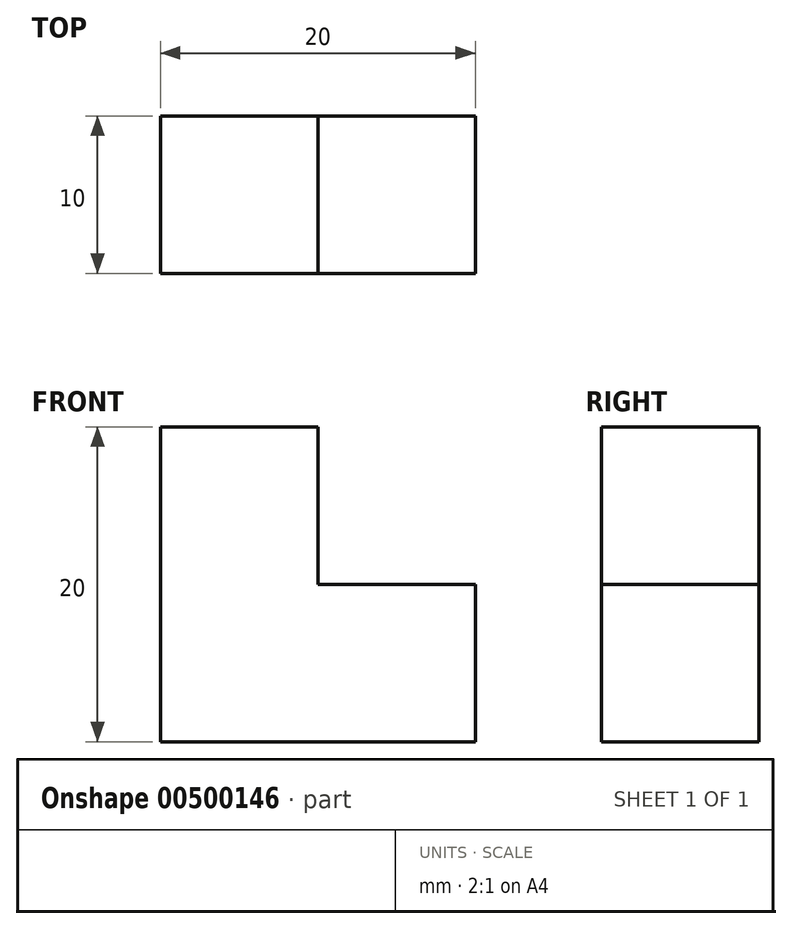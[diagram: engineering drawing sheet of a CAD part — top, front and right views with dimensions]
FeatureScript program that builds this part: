
annotation { "Feature Type Name" : "Feature", "Feature Type Description" : "" }
export const myFeature = defineFeature(function(context is Context, id is Id, definition is map)
    precondition{}
    {
        {
            var Q0;
            Q0=qCreatedBy(makeId("Front.planeOp"),FACE);
            var sketch = newSketch(context, id + "F0", { "sketchPlane" : qUnion([Q0])});
            skLineSegment(sketch, "E0", {"start": v(-26.71, 10) * mm, "end": v(-26.71, -10) * mm});
            skLineSegment(sketch, "E1", {"start": v(-26.71, -10) * mm, "end": v(-6.71, -10) * mm});
            skLineSegment(sketch, "E2", {"start": v(-6.71, -10) * mm, "end": v(-6.71, 0) * mm});
            skLineSegment(sketch, "E3", {"start": v(-6.71, 0) * mm, "end": v(-16.71, 0) * mm});
            skLineSegment(sketch, "E4", {"start": v(-16.71, 0) * mm, "end": v(-16.71, 10) * mm});
            skLineSegment(sketch, "E5", {"start": v(-16.71, 10) * mm, "end": v(-26.71, 10) * mm});
            skSolve(sketch);
        }
        {
            var Q0;
            Q0=makeQuery(id+"F0.imprint","IMPRINT",FACE,{"disambiguationData":[TD([[makeQuery(id+"F0.imprint","IMPRINT",EDGE,{"derivedFrom":sQuery(id+"F0.wireOp",EDGE,"E0")}),1.0]])]});
            extrude(context, id + "F1", {"entities" : qUnion([Q0]), "depth" : 10 * mm});
        }
    });
